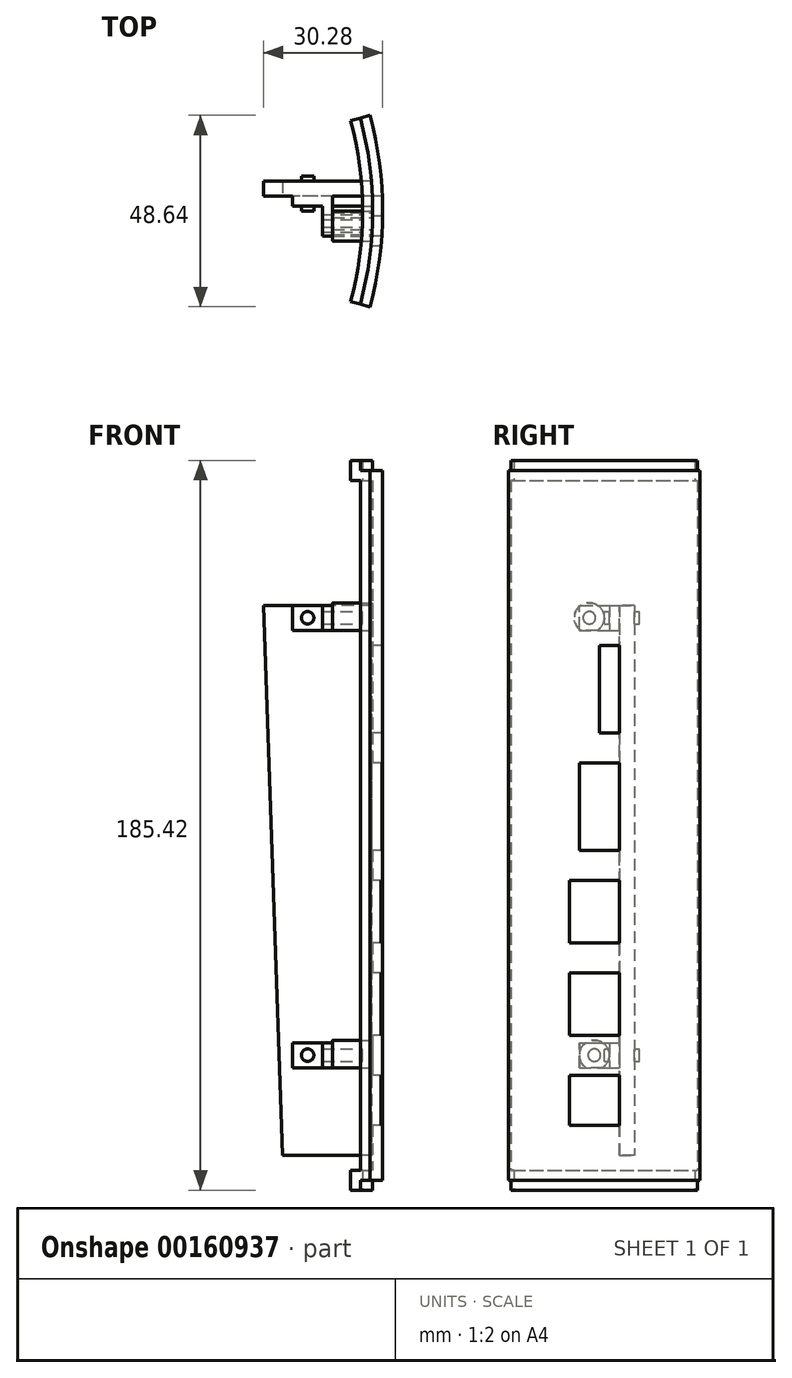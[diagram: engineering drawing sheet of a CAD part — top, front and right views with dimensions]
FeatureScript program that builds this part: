
annotation { "Feature Type Name" : "Feature", "Feature Type Description" : "" }
export const myFeature = defineFeature(function(context is Context, id is Id, definition is map)
    precondition{}
    {
        {
            var Q0;
            Q0=qCreatedBy(makeId("Front.planeOp"),FACE);
            var sketch = newSketch(context, id + "F0", { "sketchPlane" : qUnion([Q0])});
            skLineSegment(sketch, "E0.bottom", {"start": v(0, 146.05) * mm, "end": v(-27.74, 146.05) * mm});
            skLineSegment(sketch, "E0.top", {"start": v(0, 6.35) * mm, "end": v(-22.86, 6.35) * mm});
            skLineSegment(sketch, "E0.left", {"start": v(0, 146.05) * mm, "end": v(0, 6.35) * mm});
            skPoint(sketch, "E0.middle", {"position": v(0, 0) * mm});
            skLineSegment(sketch, "E1.top", {"start": v(2.54, 113.67) * mm, "end": v(-22.86, 113.67) * mm});
            skLineSegment(sketch, "E1.left", {"start": v(2.54, 135.89) * mm, "end": v(2.54, 113.66) * mm});
            skLineSegment(sketch, "E1.right", {"start": v(-22.86, 135.89) * mm, "end": v(-22.86, 113.66) * mm});
            skLineSegment(sketch, "E2.bottom", {"start": v(2.54, 106.05) * mm, "end": v(-19.69, 106.05) * mm});
            skLineSegment(sketch, "E2.top", {"start": v(2.54, 83.82) * mm, "end": v(-19.69, 83.82) * mm});
            skLineSegment(sketch, "E2.left", {"start": v(2.54, 106.04) * mm, "end": v(2.54, 83.82) * mm});
            skLineSegment(sketch, "E2.right", {"start": v(-19.69, 106.04) * mm, "end": v(-19.69, 83.82) * mm});
            skLineSegment(sketch, "E3.bottom", {"start": v(2.54, 76.2) * mm, "end": v(-15.88, 76.2) * mm});
            skLineSegment(sketch, "E3.top", {"start": v(2.54, 60.32) * mm, "end": v(-15.88, 60.32) * mm});
            skLineSegment(sketch, "E3.left", {"start": v(2.54, 76.2) * mm, "end": v(2.54, 60.32) * mm});
            skLineSegment(sketch, "E3.right", {"start": v(-15.88, 76.2) * mm, "end": v(-15.88, 60.32) * mm});
            skLineSegment(sketch, "E4.bottom", {"start": v(2.54, 52.7) * mm, "end": v(-13.34, 52.7) * mm});
            skLineSegment(sketch, "E4.top", {"start": v(2.54, 36.83) * mm, "end": v(-13.34, 36.83) * mm});
            skLineSegment(sketch, "E4.left", {"start": v(2.54, 52.7) * mm, "end": v(2.54, 36.83) * mm});
            skLineSegment(sketch, "E4.right", {"start": v(-13.34, 52.7) * mm, "end": v(-13.34, 36.83) * mm});
            skLineSegment(sketch, "E5.bottom", {"start": v(2.54, 26.67) * mm, "end": v(-16.51, 26.67) * mm});
            skLineSegment(sketch, "E5.top", {"start": v(2.54, 13.97) * mm, "end": v(-16.51, 13.97) * mm});
            skLineSegment(sketch, "E5.left", {"start": v(2.54, 26.67) * mm, "end": v(2.54, 13.97) * mm});
            skLineSegment(sketch, "E5.right", {"start": v(-16.51, 26.67) * mm, "end": v(-16.51, 13.97) * mm});
            skLineSegment(sketch, "E6", {"start": v(-22.86, 135.9) * mm, "end": v(2.54, 135.9) * mm});
            skLineSegment(sketch, "E7", {"start": v(-22.86, 6.35) * mm, "end": v(-27.74, 146.05) * mm});
            skLineSegment(sketch, "E8.bottom", {"start": v(-12.7, 139.7) * mm, "end": v(-20.32, 139.7) * mm});
            skLineSegment(sketch, "E8.top", {"start": v(-12.7, 146.05) * mm, "end": v(-22.86, 146.05) * mm});
            skLineSegment(sketch, "E8.left", {"start": v(-12.7, 139.7) * mm, "end": v(-12.7, 146.05) * mm});
            skLineSegment(sketch, "E9.bottom", {"start": v(-12.7, 28.57) * mm, "end": v(-20.32, 28.57) * mm});
            skLineSegment(sketch, "E9.top", {"start": v(-12.7, 34.92) * mm, "end": v(-20.32, 34.92) * mm});
            skLineSegment(sketch, "E9.left", {"start": v(-12.7, 28.57) * mm, "end": v(-12.7, 34.92) * mm});
            skLineSegment(sketch, "E10", {"start": v(-20.32, 34.92) * mm, "end": v(-20.32, 28.57) * mm});
            skLineSegment(sketch, "E11", {"start": v(-20.32, 146.05) * mm, "end": v(-20.32, 139.7) * mm});
            skCircle(sketch, "E12", {"center": v(-16.51, 31.75) * mm, "radius": 1.59 * mm});
            skCircle(sketch, "E13", {"center": v(-16.51, 142.87) * mm, "radius": 1.59 * mm});
            skPoint(sketch, "E14", {"position": v(0, 36.83) * mm});
            skPoint(sketch, "E15", {"position": v(0, 26.67) * mm});
            skPoint(sketch, "E16", {"position": v(0, 31.75) * mm});
            skLineSegment(sketch, "E17", {"start": v(0, 31.75) * mm, "end": v(-37.76, 31.75) * mm, "construction": true});
            skPoint(sketch, "E18", {"position": v(-12.7, 31.75) * mm});
            skPoint(sketch, "E19", {"position": v(-12.7, 142.87) * mm});
            skLineSegment(sketch, "E20", {"start": v(-2.37, 142.87) * mm, "end": v(-23.9, 142.87) * mm, "construction": true});
            skPoint(sketch, "E20.endSnap0", {"position": v(-22.86, 142.87) * mm});
            skLineSegment(sketch, "E21", {"start": v(-12.7, 139.7) * mm, "end": v(-10.16, 139.7) * mm});
            skLineSegment(sketch, "E22", {"start": v(-10.16, 139.7) * mm, "end": v(-10.16, 146.05) * mm});
            skLineSegment(sketch, "E23", {"start": v(-12.7, 34.92) * mm, "end": v(-10.16, 34.92) * mm});
            skLineSegment(sketch, "E24", {"start": v(-10.16, 34.92) * mm, "end": v(-10.16, 28.57) * mm});
            skLineSegment(sketch, "E25", {"start": v(-10.16, 28.57) * mm, "end": v(-12.7, 28.57) * mm});
            skSolve(sketch);
        }
        {
            var Q0;
            {var subQ5=sQuery(id+"F0.wireOp",EDGE,"E1.right");Q0=makeQuery(id+"F0.imprint","IMPRINT",FACE,{"disambiguationData":[TD([[makeQuery(id+"F0.imprint","IMPRINT",EDGE,{"derivedFrom":subQ5}),1.0]])]});}
            var Q1;
            {var subQ5=sQuery(id+"F0.wireOp",EDGE,"E4.right");Q1=makeQuery(id+"F0.imprint","IMPRINT",FACE,{"disambiguationData":[TD([[makeQuery(id+"F0.imprint","IMPRINT",EDGE,{"derivedFrom":subQ5}),1.0]])]});}
            var Q2;
            {var subQ5=sQuery(id+"F0.wireOp",EDGE,"E5.right");Q2=makeQuery(id+"F0.imprint","IMPRINT",FACE,{"disambiguationData":[TD([[makeQuery(id+"F0.imprint","IMPRINT",EDGE,{"derivedFrom":subQ5}),1.0]])]});}
            var Q3;
            {var subQ5=sQuery(id+"F0.wireOp",EDGE,"E2.right");Q3=makeQuery(id+"F0.imprint","IMPRINT",FACE,{"disambiguationData":[TD([[makeQuery(id+"F0.imprint","IMPRINT",EDGE,{"derivedFrom":subQ5}),1.0]])]});}
            var Q4;
            {var subQ5=sQuery(id+"F0.wireOp",EDGE,"E3.right");Q4=makeQuery(id+"F0.imprint","IMPRINT",FACE,{"disambiguationData":[TD([[makeQuery(id+"F0.imprint","IMPRINT",EDGE,{"derivedFrom":subQ5}),1.0]])]});}
            var Q5;
            {var subQ23=sQuery(id+"F0.wireOp",EDGE,"E0.bottom");Q5=makeQuery(id+"F0.imprint","IMPRINT",FACE,{"disambiguationData":[TD([[makeQuery(id+"F0.imprint","IMPRINT",EDGE,{"derivedFrom":subQ23}),1.0]])]});}
            var Q6;
            {var subQ5=sQuery(id+"F0.wireOp",EDGE,"E8.left");Q6=makeQuery(id+"F0.imprint","IMPRINT",FACE,{"disambiguationData":[TD([[makeQuery(id+"F0.imprint","IMPRINT",EDGE,{"derivedFrom":subQ5}),1.0]])]});}
            var Q7;
            {var subQ5=sQuery(id+"F0.wireOp",EDGE,"E9.left");Q7=makeQuery(id+"F0.imprint","IMPRINT",FACE,{"disambiguationData":[TD([[makeQuery(id+"F0.imprint","IMPRINT",EDGE,{"derivedFrom":subQ5}),1.0]])]});}
            var Q8;
            Q8=makeQuery(id+"F0.imprint","IMPRINT",FACE,{"disambiguationData":[TD([[makeQuery(id+"F0.imprint","IMPRINT",EDGE,{"derivedFrom":sQuery(id+"F0.wireOp",EDGE,"E12")}),1.0]])]});
            var Q9;
            Q9=makeQuery(id+"F0.imprint","IMPRINT",FACE,{"disambiguationData":[TD([[makeQuery(id+"F0.imprint","IMPRINT",EDGE,{"derivedFrom":sQuery(id+"F0.wireOp",EDGE,"E13")}),1.0]])]});
            var Q10;
            {var subQ0=sQuery(id+"F0.wireOp",EDGE,"E9.right");Q10=makeQuery(id+"F0.imprint","IMPRINT",FACE,{"disambiguationData":[TD([[makeQuery(id+"F0.imprint","IMPRINT",EDGE,{"derivedFrom":subQ0}),-1.0]])]});}
            var Q11;
            {var subQ0=sQuery(id+"F0.wireOp",EDGE,"E8.right");Q11=makeQuery(id+"F0.imprint","IMPRINT",FACE,{"disambiguationData":[TD([[makeQuery(id+"F0.imprint","IMPRINT",EDGE,{"derivedFrom":subQ0}),-1.0]])]});}
            var Q12;
            Q12=makeQuery(id+"F0.imprint","IMPRINT",FACE,{"disambiguationData":[TD([[makeQuery(id+"F0.imprint","IMPRINT",EDGE,{"derivedFrom":sQuery(id+"F0.wireOp",EDGE,"E9.left")}),-1.0]])]});
            var Q13;
            {var subQ0=sQuery(id+"F0.wireOp",EDGE,"E8.left");Q13=makeQuery(id+"F0.imprint","IMPRINT",FACE,{"disambiguationData":[TD([[makeQuery(id+"F0.imprint","IMPRINT",EDGE,{"derivedFrom":subQ0}),-1.0]])]});}
            extrude(context, id + "F1", {"entities" : qUnion([Q0, Q1, Q2, Q3, Q4, Q5, Q6, Q7, Q8, Q9, Q10, Q11, Q12, Q13]), "oppositeDirection" : true, "depth" : 3.8 * mm});
        }
        {
            var Q0;
            {var subQ5=sQuery(id+"F0.wireOp",EDGE,"E1.right");Q0=makeQuery(id+"F0.imprint","IMPRINT",FACE,{"disambiguationData":[TD([[makeQuery(id+"F0.imprint","IMPRINT",EDGE,{"derivedFrom":subQ5}),1.0]])]});}
            var Q1;
            {var subQ5=sQuery(id+"F0.wireOp",EDGE,"E1.left");Q1=makeQuery(id+"F0.imprint","IMPRINT",FACE,{"disambiguationData":[TD([[makeQuery(id+"F0.imprint","IMPRINT",EDGE,{"derivedFrom":subQ5}),-1.0]])]});}
            extrude(context, id + "F2", {"entities" : qUnion([Q0, Q1]), "operationType" : NewBodyOperationType.ADD, "depth" : 5.08 * mm});
        }
        {
            var Q0;
            Q0=makeQuery(id+"F0.imprint","IMPRINT",FACE,{"disambiguationData":[TD([[makeQuery(id+"F0.imprint","IMPRINT",EDGE,{"derivedFrom":sQuery(id+"F0.wireOp",EDGE,"E2.bottom")}),1.0]])]});
            extrude(context, id + "F3", {"entities" : qUnion([Q0]), "operationType" : NewBodyOperationType.ADD, "depth" : 10.16 * mm});
        }
        {
            var Q0;
            Q0=makeQuery(id+"F0.imprint","IMPRINT",FACE,{"disambiguationData":[TD([[makeQuery(id+"F0.imprint","IMPRINT",EDGE,{"derivedFrom":sQuery(id+"F0.wireOp",EDGE,"E3.bottom")}),1.0]])]});
            var Q1;
            Q1=makeQuery(id+"F0.imprint","IMPRINT",FACE,{"disambiguationData":[TD([[makeQuery(id+"F0.imprint","IMPRINT",EDGE,{"derivedFrom":sQuery(id+"F0.wireOp",EDGE,"E4.bottom")}),1.0]])]});
            var Q2;
            Q2=makeQuery(id+"F0.imprint","IMPRINT",FACE,{"disambiguationData":[TD([[makeQuery(id+"F0.imprint","IMPRINT",EDGE,{"derivedFrom":sQuery(id+"F0.wireOp",EDGE,"E5.bottom")}),1.0]])]});
            extrude(context, id + "F4", {"entities" : qUnion([Q0, Q1, Q2]), "operationType" : NewBodyOperationType.ADD, "depth" : 12.7 * mm});
        }
        {
            var Q0;
            Q0=makeQuery(id+"F4.opExtrude","SWEPT_FACE",FACE,{"disambiguationData":[OSD([sQuery(id+"F0.wireOp",EDGE,"E5.left")])]});
            var sketch = newSketch(context, id + "F5", { "sketchPlane" : qUnion([Q0])});
            skLineSegment(sketch, "E26.bottom", {"start": v(-10.58, 39.32) * mm, "end": v(-2.21, 39.32) * mm});
            skLineSegment(sketch, "E26.top", {"start": v(-10.58, 50.16) * mm, "end": v(-2.21, 50.16) * mm});
            skLineSegment(sketch, "E26.left", {"start": v(-10.58, 39.32) * mm, "end": v(-10.58, 50.16) * mm});
            skLineSegment(sketch, "E26.right", {"start": v(-2.21, 39.32) * mm, "end": v(-2.21, 50.16) * mm});
            skLineSegment(sketch, "E27.bottom", {"start": v(-8.75, 62.7) * mm, "end": v(-3.36, 62.7) * mm});
            skLineSegment(sketch, "E27.top", {"start": v(-8.75, 73.66) * mm, "end": v(-3.36, 73.66) * mm});
            skLineSegment(sketch, "E27.left", {"start": v(-8.75, 62.7) * mm, "end": v(-8.75, 73.66) * mm});
            skLineSegment(sketch, "E27.right", {"start": v(-3.36, 62.7) * mm, "end": v(-3.36, 73.66) * mm});
            skLineSegment(sketch, "E28.bottom", {"start": v(-6.74, 86.68) * mm, "end": v(-4.13, 86.68) * mm});
            skLineSegment(sketch, "E28.top", {"start": v(-6.74, 103.5) * mm, "end": v(-4.13, 103.5) * mm});
            skLineSegment(sketch, "E28.left", {"start": v(-6.74, 86.68) * mm, "end": v(-6.74, 103.5) * mm});
            skLineSegment(sketch, "E28.right", {"start": v(-4.13, 86.68) * mm, "end": v(-4.13, 103.5) * mm});
            skLineSegment(sketch, "E29.bottom", {"start": v(-2.9, 115.48) * mm, "end": v(-1.76, 115.48) * mm});
            skLineSegment(sketch, "E29.top", {"start": v(-2.9, 133.35) * mm, "end": v(-1.76, 133.35) * mm});
            skLineSegment(sketch, "E29.left", {"start": v(-2.9, 115.48) * mm, "end": v(-2.9, 133.35) * mm});
            skLineSegment(sketch, "E29.right", {"start": v(-1.76, 115.48) * mm, "end": v(-1.76, 133.35) * mm});
            skCircle(sketch, "E30", {"center": v(-6.52, 20.46) * mm, "radius": 4.3 * mm});
            skLineSegment(sketch, "E31.0.0", {"start": v(0, 113.67) * mm, "end": v(0, 135.89) * mm});
            skLineSegment(sketch, "E31.0.1", {"start": v(0, 135.89) * mm, "end": v(-5.08, 135.89) * mm});
            skLineSegment(sketch, "E31.0.2", {"start": v(-5.08, 135.89) * mm, "end": v(-5.08, 113.67) * mm});
            skLineSegment(sketch, "E31.0.3", {"start": v(-5.08, 113.67) * mm, "end": v(0, 113.67) * mm});
            skLineSegment(sketch, "E32.0.0", {"start": v(0, 83.82) * mm, "end": v(0, 106.05) * mm});
            skLineSegment(sketch, "E32.0.1", {"start": v(0, 106.05) * mm, "end": v(-10.16, 106.05) * mm});
            skLineSegment(sketch, "E32.0.2", {"start": v(-10.16, 106.05) * mm, "end": v(-10.16, 83.82) * mm});
            skLineSegment(sketch, "E32.0.3", {"start": v(-10.16, 83.82) * mm, "end": v(0, 83.82) * mm});
            skLineSegment(sketch, "E33.0.0", {"start": v(0, 60.32) * mm, "end": v(0, 76.2) * mm});
            skLineSegment(sketch, "E33.0.1", {"start": v(0, 76.2) * mm, "end": v(-12.7, 76.2) * mm});
            skLineSegment(sketch, "E33.0.2", {"start": v(-12.7, 76.2) * mm, "end": v(-12.7, 60.32) * mm});
            skLineSegment(sketch, "E33.0.3", {"start": v(-12.7, 60.32) * mm, "end": v(0, 60.32) * mm});
            skLineSegment(sketch, "E34.0.0", {"start": v(0, 36.83) * mm, "end": v(0, 52.7) * mm});
            skLineSegment(sketch, "E34.0.1", {"start": v(0, 52.7) * mm, "end": v(-12.7, 52.7) * mm});
            skLineSegment(sketch, "E34.0.2", {"start": v(-12.7, 52.7) * mm, "end": v(-12.7, 36.83) * mm});
            skLineSegment(sketch, "E34.0.3", {"start": v(-12.7, 36.83) * mm, "end": v(0, 36.83) * mm});
            skLineSegment(sketch, "E35.0.0", {"start": v(0, 13.97) * mm, "end": v(0, 26.67) * mm});
            skLineSegment(sketch, "E35.0.1", {"start": v(0, 26.67) * mm, "end": v(-12.7, 26.67) * mm});
            skLineSegment(sketch, "E35.0.2", {"start": v(-12.7, 26.67) * mm, "end": v(-12.7, 13.97) * mm});
            skLineSegment(sketch, "E35.0.3", {"start": v(-12.7, 13.97) * mm, "end": v(0, 13.97) * mm});
            skSolve(sketch);
        }
        {
            var Q0;
            Q0=makeQuery(id+"F5.imprint","IMPRINT",FACE,{"disambiguationData":[TD([[makeQuery(id+"F5.imprint","IMPRINT",EDGE,{"derivedFrom":sQuery(id+"F5.wireOp",EDGE,"QsPSDZzv-uLEy-goyq-KVDh-X1oqXHNKHxUB.bottom")}),1.0]])]});
            var Q1;
            Q1=makeQuery(id+"F5.imprint","IMPRINT",FACE,{"disambiguationData":[TD([[makeQuery(id+"F5.imprint","IMPRINT",EDGE,{"derivedFrom":sQuery(id+"F5.wireOp",EDGE,"E26.bottom")}),1.0]])]});
            var Q2;
            Q2=makeQuery(id+"F5.imprint","IMPRINT",FACE,{"disambiguationData":[TD([[makeQuery(id+"F5.imprint","IMPRINT",EDGE,{"derivedFrom":sQuery(id+"F5.wireOp",EDGE,"E27.bottom")}),1.0]])]});
            var Q3;
            Q3=makeQuery(id+"F5.imprint","IMPRINT",FACE,{"disambiguationData":[TD([[makeQuery(id+"F5.imprint","IMPRINT",EDGE,{"derivedFrom":sQuery(id+"F5.wireOp",EDGE,"E28.bottom")}),1.0]])]});
            var Q4;
            Q4=makeQuery(id+"F5.imprint","IMPRINT",FACE,{"disambiguationData":[TD([[makeQuery(id+"F5.imprint","IMPRINT",EDGE,{"derivedFrom":sQuery(id+"F5.wireOp",EDGE,"E29.bottom")}),1.0]])]});
            var Q5;
            Q5=makeQuery(id+"F5.imprint","IMPRINT",FACE,{"disambiguationData":[TD([[makeQuery(id+"F5.imprint","IMPRINT",EDGE,{"derivedFrom":sQuery(id+"F5.wireOp",EDGE,"E30")}),1.0]])]});
            extrude(context, id + "F6", {"entities" : qUnion([Q0, Q1, Q2, Q3, Q4, Q5]), "operationType" : NewBodyOperationType.REMOVE, "oppositeDirection" : true, "depth" : 12.7 * mm});
        }
        {
            var Q0;
            {var subQ5=sQuery(id+"F0.wireOp",EDGE,"E8.left");Q0=makeQuery(id+"F0.imprint","IMPRINT",FACE,{"disambiguationData":[TD([[makeQuery(id+"F0.imprint","IMPRINT",EDGE,{"derivedFrom":subQ5}),1.0]])]});}
            var Q1;
            {var subQ5=sQuery(id+"F0.wireOp",EDGE,"E11");Q1=makeQuery(id+"F0.imprint","IMPRINT",FACE,{"disambiguationData":[TD([[makeQuery(id+"F0.imprint","IMPRINT",EDGE,{"derivedFrom":subQ5}),1.0]])]});}
            var Q2;
            {var subQ0=sQuery(id+"F0.wireOp",EDGE,"E8.right");Q2=makeQuery(id+"F0.imprint","IMPRINT",FACE,{"disambiguationData":[TD([[makeQuery(id+"F0.imprint","IMPRINT",EDGE,{"derivedFrom":subQ0}),-1.0]])]});}
            var Q3;
            {var subQ5=sQuery(id+"F0.wireOp",EDGE,"E9.left");Q3=makeQuery(id+"F0.imprint","IMPRINT",FACE,{"disambiguationData":[TD([[makeQuery(id+"F0.imprint","IMPRINT",EDGE,{"derivedFrom":subQ5}),1.0]])]});}
            var Q4;
            {var subQ5=sQuery(id+"F0.wireOp",EDGE,"E10");Q4=makeQuery(id+"F0.imprint","IMPRINT",FACE,{"disambiguationData":[TD([[makeQuery(id+"F0.imprint","IMPRINT",EDGE,{"derivedFrom":subQ5}),1.0]])]});}
            var Q5;
            {var subQ0=sQuery(id+"F0.wireOp",EDGE,"E9.right");Q5=makeQuery(id+"F0.imprint","IMPRINT",FACE,{"disambiguationData":[TD([[makeQuery(id+"F0.imprint","IMPRINT",EDGE,{"derivedFrom":subQ0}),-1.0]])]});}
            extrude(context, id + "F7", {"entities" : qUnion([Q0, Q1, Q2, Q3, Q4, Q5]), "operationType" : NewBodyOperationType.ADD, "depth" : 2.54 * mm});
        }
        {
            var Q0;
            {var subQ0=sQuery(id+"F0.wireOp",EDGE,"E8.left");Q0=makeQuery(id+"F0.imprint","IMPRINT",FACE,{"disambiguationData":[TD([[makeQuery(id+"F0.imprint","IMPRINT",EDGE,{"derivedFrom":subQ0}),-1.0]])]});}
            var Q1;
            Q1=makeQuery(id+"F0.imprint","IMPRINT",FACE,{"disambiguationData":[TD([[makeQuery(id+"F0.imprint","IMPRINT",EDGE,{"derivedFrom":sQuery(id+"F0.wireOp",EDGE,"E9.left")}),-1.0]])]});
            extrude(context, id + "F8", {"entities" : qUnion([Q0, Q1]), "operationType" : NewBodyOperationType.ADD, "depth" : 10.16 * mm});
        }
        {
            var Q0;
            Q0=makeQuery(id+"F0.imprint","IMPRINT",FACE,{"disambiguationData":[TD([[makeQuery(id+"F0.imprint","IMPRINT",EDGE,{"derivedFrom":sQuery(id+"F0.wireOp",EDGE,"E13")}),1.0]])]});
            var Q1;
            Q1=makeQuery(id+"F0.imprint","IMPRINT",FACE,{"disambiguationData":[TD([[makeQuery(id+"F0.imprint","IMPRINT",EDGE,{"derivedFrom":sQuery(id+"F0.wireOp",EDGE,"E12")}),1.0]])]});
            extrude(context, id + "F9", {"entities" : qUnion([Q0, Q1]), "operationType" : NewBodyOperationType.ADD, "depth" : 3.8 * mm, "hasSecondDirection" : true, "secondDirectionOppositeDirection" : true, "secondDirectionDepth" : 5.08 * mm});
        }
        {
            var Q0;
            Q0=qCreatedBy(makeId("Right.planeOp"),FACE);
            var sketch = newSketch(context, id + "F10", { "sketchPlane" : qUnion([Q0])});
            skLineSegment(sketch, "E36.0.0", {"start": v(0, 139.7) * mm, "end": v(0, 146.05) * mm});
            skLineSegment(sketch, "E36.0.1", {"start": v(-10.16, 139.7) * mm, "end": v(0, 139.7) * mm});
            skLineSegment(sketch, "E36.0.2", {"start": v(-10.16, 146.05) * mm, "end": v(-10.16, 139.7) * mm});
            skLineSegment(sketch, "E36.0.3", {"start": v(0, 146.05) * mm, "end": v(-10.16, 146.05) * mm});
            skLineSegment(sketch, "E37.0.0", {"start": v(0, 28.57) * mm, "end": v(0, 34.92) * mm});
            skLineSegment(sketch, "E37.0.1", {"start": v(-10.16, 28.57) * mm, "end": v(0, 28.57) * mm});
            skLineSegment(sketch, "E37.0.2", {"start": v(-10.16, 34.92) * mm, "end": v(-10.16, 28.57) * mm});
            skLineSegment(sketch, "E37.0.3", {"start": v(0, 34.92) * mm, "end": v(-10.16, 34.92) * mm});
            skPoint(sketch, "E38", {"position": v(-10.16, 142.87) * mm});
            skLineSegment(sketch, "E39", {"start": v(0, 142.87) * mm, "end": v(-10.16, 142.87) * mm, "construction": true});
            skCircle(sketch, "E40", {"center": v(-7.62, 142.87) * mm, "radius": 1.59 * mm});
            skCircle(sketch, "E41", {"center": v(-7.62, 142.87) * mm, "radius": 3.81 * mm});
            skPoint(sketch, "E42", {"position": v(-10.16, 31.75) * mm});
            skLineSegment(sketch, "E43", {"start": v(0, 31.75) * mm, "end": v(-10.16, 31.75) * mm, "construction": true});
            skCircle(sketch, "E44", {"center": v(-6.35, 31.75) * mm, "radius": 1.59 * mm});
            skCircle(sketch, "E45", {"center": v(-6.35, 31.75) * mm, "radius": 3.81 * mm});
            skSolve(sketch);
        }
        {
            var Q0;
            Q0=makeQuery(id+"F10.imprint","IMPRINT",FACE,{"disambiguationData":[TD([[makeQuery(id+"F10.imprint","IMPRINT",EDGE,{"derivedFrom":sQuery(id+"F10.wireOp",EDGE,"mAwodLHo-5CJ7-BU8g-Eq2X-gMBFYanYIdpS")}),1.0]])]});
            var Q1;
            {var subQ0=sQuery(id+"F10.wireOp",EDGE,"BFzIXqao-JbxE-Ypqr-w9Nd-hP7NoaJlb3yi");var subQ1=sQuery(id+"F10.wireOp",EDGE,"04AyWxKv-bo47-RNZc-UAjW-Hn0S6AFtiVpr");var subQ2=makeQuery(id+"F10.imprint","INTERSECT",VERTEX,{"disambiguationData":[OD(0.0)],"derivedFrom":[subQ1,subQ0]});Q1=makeQuery(id+"F10.imprint","IMPRINT",FACE,{"disambiguationData":[TD([[makeQuery(id+"F10.imprint","IMPRINT",EDGE,{"disambiguationData":[TD([[subQ2,1.0]])],"derivedFrom":subQ1}),1.0]])]});}
            var Q2;
            {var subQ0=sQuery(id+"F10.wireOp",EDGE,"9as04cPz-zgJ7-VkpZ-YAaS-p6B9O8Tkpz6i");var subQ1=sQuery(id+"F10.wireOp",EDGE,"04AyWxKv-bo47-RNZc-UAjW-Hn0S6AFtiVpr");var subQ2=makeQuery(id+"F10.imprint","INTERSECT",VERTEX,{"disambiguationData":[OD(0.0)],"derivedFrom":[subQ1,subQ0]});Q2=makeQuery(id+"F10.imprint","IMPRINT",FACE,{"disambiguationData":[TD([[makeQuery(id+"F10.imprint","IMPRINT",EDGE,{"disambiguationData":[TD([[subQ2,1.0]])],"derivedFrom":subQ1}),1.0]])]});}
            var Q3;
            {var subQ0=sQuery(id+"F10.wireOp",EDGE,"9as04cPz-zgJ7-VkpZ-YAaS-p6B9O8Tkpz6i");var subQ1=sQuery(id+"F10.wireOp",EDGE,"04AyWxKv-bo47-RNZc-UAjW-Hn0S6AFtiVpr");var subQ2=makeQuery(id+"F10.imprint","INTERSECT",VERTEX,{"disambiguationData":[OD(0.0)],"derivedFrom":[subQ1,subQ0]});Q3=makeQuery(id+"F10.imprint","IMPRINT",FACE,{"disambiguationData":[TD([[makeQuery(id+"F10.imprint","IMPRINT",EDGE,{"disambiguationData":[TD([[subQ2,-1.0]])],"derivedFrom":subQ1}),1.0]])]});}
            var Q4;
            {var subQ0=sQuery(id+"F10.wireOp",EDGE,"BFzIXqao-JbxE-Ypqr-w9Nd-hP7NoaJlb3yi");var subQ1=sQuery(id+"F10.wireOp",EDGE,"04AyWxKv-bo47-RNZc-UAjW-Hn0S6AFtiVpr");var subQ2=makeQuery(id+"F10.imprint","INTERSECT",VERTEX,{"disambiguationData":[OD(1.0)],"derivedFrom":[subQ1,subQ0]});Q4=makeQuery(id+"F10.imprint","IMPRINT",FACE,{"disambiguationData":[TD([[makeQuery(id+"F10.imprint","IMPRINT",EDGE,{"disambiguationData":[TD([[subQ2,-1.0]])],"derivedFrom":subQ1}),1.0]])]});}
            var Q5;
            Q5=makeQuery(id+"F10.imprint","IMPRINT",FACE,{"disambiguationData":[TD([[makeQuery(id+"F10.imprint","IMPRINT",EDGE,{"derivedFrom":sQuery(id+"F10.wireOp",EDGE,"E44")}),1.0]])]});
            var Q6;
            Q6=makeQuery(id+"F10.imprint","IMPRINT",FACE,{"disambiguationData":[TD([[makeQuery(id+"F10.imprint","IMPRINT",EDGE,{"derivedFrom":sQuery(id+"F10.wireOp",EDGE,"E40")}),1.0]])]});
            extrude(context, id + "F11", {"entities" : qUnion([Q0, Q1, Q2, Q3, Q4, Q5, Q6]), "operationType" : NewBodyOperationType.REMOVE, "oppositeDirection" : true, "depth" : 25.4 * mm});
        }
        {
            var Q0;
            Q0=qCreatedBy(makeId("Top.planeOp"),FACE);
            var sketch = newSketch(context, id + "F12", { "sketchPlane" : qUnion([Q0])});
            skCircle(sketch, "E46", {"center": v(-91.44, -3.81) * mm, "radius": 93.98 * mm});
            skCircle(sketch, "E47", {"center": v(-91.44, -3.81) * mm, "radius": 91.44 * mm});
            skCircle(sketch, "E48", {"center": v(-91.44, -3.81) * mm, "radius": 88.9 * mm});
            skLineSegment(sketch, "E49", {"start": v(-91.44, -3.81) * mm, "end": v(20.53, -3.81) * mm, "construction": true});
            skLineSegment(sketch, "E50", {"start": v(-91.44, -3.81) * mm, "end": v(-0.66, -28.13) * mm});
            skLineSegment(sketch, "E51.MirrorCS", {"start": v(-91.44, -3.81) * mm, "end": v(-0.66, 20.51) * mm});
            skPoint(sketch, "E52", {"position": v(0, -3.81) * mm});
            skSolve(sketch);
        }
        {
            var Q0;
            {var subQ0=sQuery(id+"F12.wireOp",EDGE,"E50");var subQ1=sQuery(id+"F12.wireOp",EDGE,"E46");var subQ2=makeQuery(id+"F12.imprint","INTERSECT",VERTEX,{"derivedFrom":[subQ1,subQ0]});Q0=makeQuery(id+"F12.imprint","IMPRINT",FACE,{"disambiguationData":[TD([[makeQuery(id+"F12.imprint","IMPRINT",EDGE,{"disambiguationData":[TD([[subQ2,-1.0]])],"derivedFrom":subQ1}),1.0]])]});}
            extrude(context, id + "F13", {"entities" : qUnion([Q0]), "depth" : 180.34 * mm});
        }
        {
            var Q0;
            Q0=makeQuery(id+"F5.imprint","IMPRINT",FACE,{"disambiguationData":[TD([[makeQuery(id+"F5.imprint","IMPRINT",EDGE,{"derivedFrom":sQuery(id+"F5.wireOp",EDGE,"E28.bottom")}),-1.0]])]});
            var Q1;
            Q1=makeQuery(id+"F5.imprint","IMPRINT",FACE,{"disambiguationData":[TD([[makeQuery(id+"F5.imprint","IMPRINT",EDGE,{"derivedFrom":sQuery(id+"F5.wireOp",EDGE,"E28.bottom")}),1.0]])]});
            var Q2;
            Q2=makeQuery(id+"F5.imprint","IMPRINT",FACE,{"disambiguationData":[TD([[makeQuery(id+"F5.imprint","IMPRINT",EDGE,{"derivedFrom":sQuery(id+"F5.wireOp",EDGE,"E29.bottom")}),-1.0]])]});
            var Q3;
            Q3=makeQuery(id+"F5.imprint","IMPRINT",FACE,{"disambiguationData":[TD([[makeQuery(id+"F5.imprint","IMPRINT",EDGE,{"derivedFrom":sQuery(id+"F5.wireOp",EDGE,"E29.bottom")}),1.0]])]});
            var Q4;
            Q4=makeQuery(id+"F5.imprint","IMPRINT",FACE,{"disambiguationData":[TD([[makeQuery(id+"F5.imprint","IMPRINT",EDGE,{"derivedFrom":sQuery(id+"F5.wireOp",EDGE,"E27.bottom")}),-1.0]])]});
            var Q5;
            Q5=makeQuery(id+"F5.imprint","IMPRINT",FACE,{"disambiguationData":[TD([[makeQuery(id+"F5.imprint","IMPRINT",EDGE,{"derivedFrom":sQuery(id+"F5.wireOp",EDGE,"E27.bottom")}),1.0]])]});
            var Q6;
            Q6=makeQuery(id+"F5.imprint","IMPRINT",FACE,{"disambiguationData":[TD([[makeQuery(id+"F5.imprint","IMPRINT",EDGE,{"derivedFrom":sQuery(id+"F5.wireOp",EDGE,"E26.bottom")}),-1.0]])]});
            var Q7;
            Q7=makeQuery(id+"F5.imprint","IMPRINT",FACE,{"disambiguationData":[TD([[makeQuery(id+"F5.imprint","IMPRINT",EDGE,{"derivedFrom":sQuery(id+"F5.wireOp",EDGE,"E26.bottom")}),1.0]])]});
            var Q8;
            Q8=makeQuery(id+"F5.imprint","IMPRINT",FACE,{"disambiguationData":[TD([[makeQuery(id+"F5.imprint","IMPRINT",EDGE,{"derivedFrom":sQuery(id+"F5.wireOp",EDGE,"E30")}),1.0]])]});
            var Q9;
            Q9=makeQuery(id+"F5.imprint","IMPRINT",FACE,{"disambiguationData":[TD([[makeQuery(id+"F5.imprint","IMPRINT",EDGE,{"derivedFrom":sQuery(id+"F5.wireOp",EDGE,"E30")}),-1.0]])]});
            extrude(context, id + "F14", {"entities" : qUnion([Q0, Q1, Q2, Q3, Q4, Q5, Q6, Q7, Q8, Q9]), "operationType" : NewBodyOperationType.REMOVE, "depth" : 25.4 * mm, "hasSecondDirection" : true, "secondDirectionOppositeDirection" : true, "secondDirectionDepth" : 25.4 * mm});
        }
        {
            var Q0;
            {var subQ0=sQuery(id+"F10.wireOp",EDGE,"E41");var subQ1=sQuery(id+"F10.wireOp",EDGE,"E36.0.1");var subQ2=makeQuery(id+"F10.imprint","INTERSECT",VERTEX,{"disambiguationData":[OD(0.0)],"derivedFrom":[subQ1,subQ0]});Q0=makeQuery(id+"F10.imprint","IMPRINT",FACE,{"disambiguationData":[TD([[makeQuery(id+"F10.imprint","IMPRINT",EDGE,{"disambiguationData":[TD([[subQ2,-1.0]])],"derivedFrom":subQ1}),-1.0]])]});}
            var Q1;
            Q1=makeQuery(id+"F10.imprint","IMPRINT",FACE,{"disambiguationData":[TD([[makeQuery(id+"F10.imprint","IMPRINT",EDGE,{"derivedFrom":sQuery(id+"F10.wireOp",EDGE,"E40")}),-1.0]])]});
            var Q2;
            Q2=makeQuery(id+"F10.imprint","IMPRINT",FACE,{"disambiguationData":[TD([[makeQuery(id+"F10.imprint","IMPRINT",EDGE,{"derivedFrom":sQuery(id+"F10.wireOp",EDGE,"E40")}),1.0]])]});
            var Q3;
            {var subQ0=sQuery(id+"F10.wireOp",EDGE,"E45");var subQ1=sQuery(id+"F10.wireOp",EDGE,"E37.0.1");var subQ2=makeQuery(id+"F10.imprint","INTERSECT",VERTEX,{"disambiguationData":[OD(0.0)],"derivedFrom":[subQ1,subQ0]});Q3=makeQuery(id+"F10.imprint","IMPRINT",FACE,{"disambiguationData":[TD([[makeQuery(id+"F10.imprint","IMPRINT",EDGE,{"disambiguationData":[TD([[subQ2,-1.0]])],"derivedFrom":subQ1}),-1.0]])]});}
            var Q4;
            Q4=makeQuery(id+"F10.imprint","IMPRINT",FACE,{"disambiguationData":[TD([[makeQuery(id+"F10.imprint","IMPRINT",EDGE,{"derivedFrom":sQuery(id+"F10.wireOp",EDGE,"E44")}),-1.0]])]});
            var Q5;
            {var subQ0=sQuery(id+"F10.wireOp",EDGE,"E45");var subQ1=sQuery(id+"F10.wireOp",EDGE,"E37.0.3");var subQ2=makeQuery(id+"F10.imprint","INTERSECT",VERTEX,{"disambiguationData":[OD(0.0)],"derivedFrom":[subQ1,subQ0]});Q5=makeQuery(id+"F10.imprint","IMPRINT",FACE,{"disambiguationData":[TD([[makeQuery(id+"F10.imprint","IMPRINT",EDGE,{"disambiguationData":[TD([[subQ2,-1.0]])],"derivedFrom":subQ1}),-1.0]])]});}
            var Q6;
            Q6=makeQuery(id+"F10.imprint","IMPRINT",FACE,{"disambiguationData":[TD([[makeQuery(id+"F10.imprint","IMPRINT",EDGE,{"derivedFrom":sQuery(id+"F10.wireOp",EDGE,"E44")}),1.0]])]});
            var Q7;
            {var subQ0=sQuery(id+"F10.wireOp",EDGE,"E41");var subQ1=sQuery(id+"F10.wireOp",EDGE,"E36.0.3");var subQ2=makeQuery(id+"F10.imprint","INTERSECT",VERTEX,{"disambiguationData":[OD(0.0)],"derivedFrom":[subQ1,subQ0]});Q7=makeQuery(id+"F10.imprint","IMPRINT",FACE,{"disambiguationData":[TD([[makeQuery(id+"F10.imprint","IMPRINT",EDGE,{"disambiguationData":[TD([[subQ2,-1.0]])],"derivedFrom":subQ1}),-1.0]])]});}
            var Q8;
            {var subQ0=sQuery(id+"F10.wireOp",EDGE,"E41");var subQ1=sQuery(id+"F10.wireOp",EDGE,"E36.0.2");var subQ2=makeQuery(id+"F10.imprint","INTERSECT",VERTEX,{"disambiguationData":[OD(0.0)],"derivedFrom":[subQ1,subQ0]});Q8=makeQuery(id+"F10.imprint","IMPRINT",FACE,{"disambiguationData":[TD([[makeQuery(id+"F10.imprint","IMPRINT",EDGE,{"disambiguationData":[TD([[subQ2,-1.0]])],"derivedFrom":subQ1}),-1.0]])]});}
            var Q9;
            Q9=makeQuery(id+"F8.opExtrude","SWEPT_FACE",FACE,{"disambiguationData":[OSD([sQuery(id+"F0.wireOp",EDGE,"E24")])]});
            var Q10;
            Q10=makeQuery(id+"F1.opExtrude","SWEPT_BODY",BODY,{"disambiguationData":[OSD([sQuery(id+"F0.wireOp",EDGE,"E0.bottom"),sQuery(id+"F0.wireOp",EDGE,"E0.top"),sQuery(id+"F0.wireOp",EDGE,"E0.left"),sQuery(id+"F0.wireOp",EDGE,"E7"),sQuery(id+"F0.wireOp",EDGE,"E8.top")])]});
            extrude(context, id + "F15", {"entities" : qUnion([Q0, Q1, Q2, Q3, Q4, Q5, Q6, Q7, Q8]), "operationType" : NewBodyOperationType.ADD, "endBound" : BoundingType.UP_TO_SURFACE, "oppositeDirection" : true, "endBoundEntityFace" : qUnion([Q9]), "endBoundEntityBody" : qUnion([Q10]), "depth" : 25.4 * mm, "hasSecondDirection" : true, "secondDirectionBound" : SecondDirectionBoundingType.UP_TO_NEXT, "secondDirectionOppositeDirection" : false, "secondDirectionDepth" : 25.4 * mm});
        }
        {
            var Q0;
            Q0=makeQuery(id+"F10.imprint","IMPRINT",FACE,{"disambiguationData":[TD([[makeQuery(id+"F10.imprint","IMPRINT",EDGE,{"derivedFrom":sQuery(id+"F10.wireOp",EDGE,"E40")}),1.0]])]});
            var Q1;
            Q1=makeQuery(id+"F10.imprint","IMPRINT",FACE,{"disambiguationData":[TD([[makeQuery(id+"F10.imprint","IMPRINT",EDGE,{"derivedFrom":sQuery(id+"F10.wireOp",EDGE,"E44")}),1.0]])]});
            extrude(context, id + "F16", {"entities" : qUnion([Q0, Q1]), "operationType" : NewBodyOperationType.REMOVE, "oppositeDirection" : true, "depth" : 25.4 * mm, "hasSecondDirection" : true, "secondDirectionOppositeDirection" : true, "secondDirectionDepth" : 2.54 * mm});
        }
        {
            var Q0;
            {var subQ0=sQuery(id+"F12.wireOp",EDGE,"E50");var subQ1=sQuery(id+"F12.wireOp",EDGE,"E47");var subQ2=makeQuery(id+"F12.imprint","INTERSECT",VERTEX,{"derivedFrom":[subQ1,subQ0]});Q0=makeQuery(id+"F12.imprint","IMPRINT",FACE,{"disambiguationData":[TD([[makeQuery(id+"F12.imprint","IMPRINT",EDGE,{"disambiguationData":[TD([[subQ2,-1.0]])],"derivedFrom":subQ1}),1.0]])]});}
            extrude(context, id + "F17", {"entities" : qUnion([Q0]), "operationType" : NewBodyOperationType.ADD, "depth" : 182.88 * mm, "hasSecondDirection" : true, "secondDirectionOppositeDirection" : false, "secondDirectionDepth" : 177.8 * mm});
        }
        {
            var Q0;
            {var subQ0=sQuery(id+"F12.wireOp",EDGE,"E50");var subQ1=sQuery(id+"F12.wireOp",EDGE,"E47");var subQ2=makeQuery(id+"F12.imprint","INTERSECT",VERTEX,{"derivedFrom":[subQ1,subQ0]});Q0=makeQuery(id+"F12.imprint","IMPRINT",FACE,{"disambiguationData":[TD([[makeQuery(id+"F12.imprint","IMPRINT",EDGE,{"disambiguationData":[TD([[subQ2,-1.0]])],"derivedFrom":subQ1}),1.0]])]});}
            extrude(context, id + "F18", {"entities" : qUnion([Q0]), "operationType" : NewBodyOperationType.ADD, "depth" : 2.54 * mm, "hasSecondDirection" : true, "secondDirectionOppositeDirection" : true, "secondDirectionDepth" : 2.54 * mm});
        }
    });
